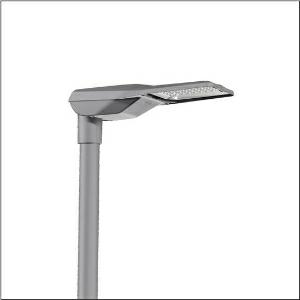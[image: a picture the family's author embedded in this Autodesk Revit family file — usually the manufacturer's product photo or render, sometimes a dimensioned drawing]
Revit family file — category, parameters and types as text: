
# Revit family: streetlight_sl_21_iq_mini___stw1_0a_5xe2e41g08jb_4c9f
name_source: partatom
category: Lighting Fixtures
units: mm (PartAtom-declared; Revit-internal decimal feet)

## family parameters
Cut with Voids When Loaded = No
Host = Face
Light Source = No
Part Type = Normal
Room Calculation Point = No
Round Connector Dimension = Use Diameter
Shared = No

## types (1)
- --- (1 x LED, 11290 lm, 71.6 W, 4000K)
    Apparent Load = 72 VA
    CIE Flux Codes = 39 75 98 100 100
    Color Rendering = 70
    Color Temperature = 4000K
    Default Elevation = 1800 mm
    Description = Streetlight SL 21 mini, mast luminaire, primary light control with lens, of PMMA, primary optical cover: cover, of toughened safety glass, transparent, light distribution: STW1.0a, light emission: direct distribution, primary light characteristic: asymmetric, installation type: post-top, side-entry, LED, High Power LED, rated luminous flux: 11.290lm, luminous efficacy: 158lm/W, light colour: 740, colour temperature: 4000K, control gear: ECG iQ, control: Street-Remote, Auto-Match, Temp-Guard, Lumen-Switch, Night-Set, Smart-Wire, Light-Fading, Desk-Remote (wireless, voltage-free reading and setting of iQ features in the workshop via application-optimized NFC function/RFID function), optimised constant luminous flux control (CLO 2.0), mains connection: 220..240V, AC, 50/60Hz, start of lifetime: 72W, end of lifetime: 75W, reduction: 33W, luminaire housing, of diecast aluminium, powder-coated, Siteco® metallic grey (DB 702S), corrosivity category C5 according to DIN EN ISO 12944, length: 628mm, width: 235mm, height: 110mm, spigot size: 60/76mm (post-top) and 42/60/76mm (side-entry), mast flange for spigot size: 42mm: 5XC10008XM4, 60mm: 5XC10008XM2, 76/60mm: 5XC10108XM1, protection rating (complete): IP66, insulation class (complete): insulation class II (safety insulation), certification: CE, ENEC, VDE, impact resistance: IK09, permissible operating ambient temperature for outdoor applications: -40..+50°C, standard-compliant lighting for roads and squares, packaging unit: 1 piece

Light Distribution: STW1.0a
    Height = 110 mm
    Lamp = 1 x LED
    Lamp Light Flux = 11290 lm
    Lamp Power = 71.6 W
    Lamp count = 1
    Length = 625 mm
    Luminous efficacy = 158 lm/W
    Manufacturer = Siteco
    ModVariant = No
    Model = 5XE2E41G08JB
    Number of Poles = 1
    OnlyDefault = Yes
    Power Factor = 1
    Product Name = Streetlight SL 21 iQ mini | STW1.0a
    Product group = mast luminaire | pylon top
    ProductGroupID = 6100
    Protection Class = Protection class II
    Protection Degree = IP 66
    RLX_Detail_Level = 1
    RlxData = <blob elided: 92441 chars, md5=23b3b0bd>
    Socket = socket
    Standby Power = 0 W
    System Light Flux = 11290 lm
    System Power = 72 W
    Type Comments = factory setting: luminous flux: 100 % | dim-lin: 254 | 746 mA
    Type Image = l_1003519.jpg
    URL = http://relux.com
    VarID = @adj_081829
    Voltage = 0 V
    Weight = 0.00 kg
    Width = 234 mm

## geometry (parser evidence)
native form markers: Blend x4, Sweep x10
no freeform markers — native parametric forms only
